# Revit family: Loading-Equipment_Dock-Levelers_Wayne-Dalton_Hydraulic-Pit-Leveler_
name_source: partatom
category: Specialty Equipment
units: mm (PartAtom-declared; Revit-internal decimal feet)

## family parameters
Cut with Voids When Loaded = Yes
Host = Face
OmniClass Number = 23.50.70.14.11
OmniClass Title = Powered Dock Levelers
Part Type = Normal
Room Calculation Point = No
Round Connector Dimension = Use Diameter
Shared = No

## types (2) — shared parameters
Default Elevation = 48 "
Length = 96 "
Main Material = Metal - Wayne Dalton - Steel
Manufacturer = Wayne Dalton
Product data url = https://www.bimobject.com
Top Plate Material = Metal - Wayne Dalton - Steel Checker Plate
URL = https://www.wayne-dalton.com
z_Real Length = 87 "

## per-type parameters (varying)
| type | Description | Model | Width |
| 6ft Wide - 8ft Length - Hydaulic Pit Leveler | H68WD Hydaulic Pit Leveler | Hydraulic Pit Leveler H68WD | 72 " |
| 7ft Wide - 8ft Length - Hydaulic Pit Leveler | H78WD Hydraulic Pit Leveler | Hydraulic Pit Leveler H78WD | 83 " |

## geometry (parser evidence)
native form markers: Sweep x11
no freeform markers — native parametric forms only
